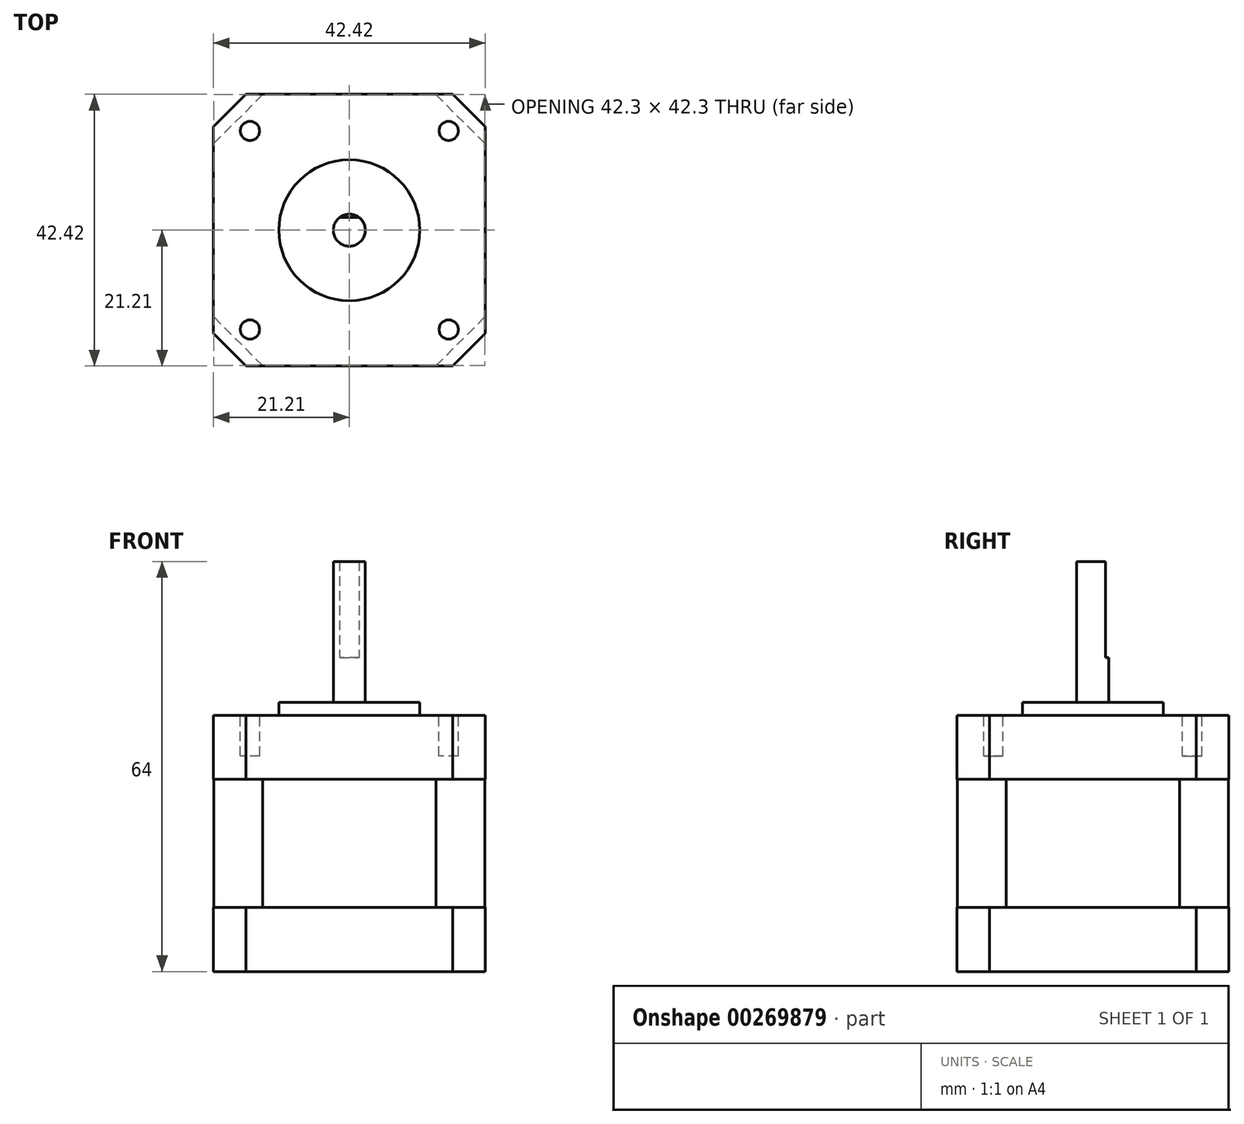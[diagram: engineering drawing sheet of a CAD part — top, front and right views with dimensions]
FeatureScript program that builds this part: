
annotation { "Feature Type Name" : "Feature", "Feature Type Description" : "" }
export const myFeature = defineFeature(function(context is Context, id is Id, definition is map)
    precondition{}
    {
        {
            var Q0;
            Q0=qCreatedBy(makeId("Top.planeOp"),FACE);
            var sketch = newSketch(context, id + "F0", { "sketchPlane" : qUnion([Q0])});
            skLineSegment(sketch, "E0.bottom", {"start": v(-21.15, 21.15) * mm, "end": v(21.15, 21.15) * mm});
            skLineSegment(sketch, "E0.top", {"start": v(-21.15, -21.15) * mm, "end": v(21.15, -21.15) * mm});
            skLineSegment(sketch, "E0.left", {"start": v(-21.15, 21.15) * mm, "end": v(-21.15, -21.15) * mm});
            skLineSegment(sketch, "E0.right", {"start": v(21.15, 21.15) * mm, "end": v(21.15, -21.15) * mm});
            skPoint(sketch, "E1", {"position": v(-21.15, 0) * mm});
            skPoint(sketch, "E2", {"position": v(0, 21.15) * mm});
            skSolve(sketch);
        }
        {
            var Q0;
            Q0=makeQuery(id+"F0.imprint","IMPRINT",FACE,{"disambiguationData":[TD([[makeQuery(id+"F0.imprint","IMPRINT",EDGE,{"derivedFrom":sQuery(id+"F0.wireOp",EDGE,"E0.bottom")}),-1.0]])]});
            extrude(context, id + "F1", {"entities" : qUnion([Q0]), "endBound" : BoundingType.SYMMETRIC, "depth" : 20 * mm});
        }
        {
            var Q0;
            Q0=makeQuery(id+"F1.opExtrude","SWEPT_EDGE",EDGE,{"disambiguationData":[OSD([sQuery(id+"F0.wireOp",EDGE,"E0.bottom"),sQuery(id+"F0.wireOp",EDGE,"E0.right")])]});
            var Q1;
            Q1=makeQuery(id+"F1.opExtrude","SWEPT_EDGE",EDGE,{"disambiguationData":[OSD([sQuery(id+"F0.wireOp",EDGE,"E0.bottom"),sQuery(id+"F0.wireOp",EDGE,"E0.left")])]});
            var Q2;
            Q2=makeQuery(id+"F1.opExtrude","SWEPT_EDGE",EDGE,{"disambiguationData":[OSD([sQuery(id+"F0.wireOp",EDGE,"E0.top"),sQuery(id+"F0.wireOp",EDGE,"E0.left")])]});
            var Q3;
            Q3=makeQuery(id+"F1.opExtrude","SWEPT_EDGE",EDGE,{"disambiguationData":[OSD([sQuery(id+"F0.wireOp",EDGE,"E0.top"),sQuery(id+"F0.wireOp",EDGE,"E0.right")])]});
            chamfer(context, id + "F2", {"entities" : qUnion([Q0, Q1, Q2, Q3]), "width" : 7.62 * mm, "tangentPropagation" : true});
        }
        {
            var Q0;
            Q0=makeQuery(id+"F1.opExtrude","CAP_FACE",FACE,{"disambiguationData":[OSD([sQuery(id+"F0.wireOp",EDGE,"E0.bottom"),sQuery(id+"F0.wireOp",EDGE,"E0.top"),sQuery(id+"F0.wireOp",EDGE,"E0.left"),sQuery(id+"F0.wireOp",EDGE,"E0.right")])],"isStart":false});
            var sketch = newSketch(context, id + "F3", { "sketchPlane" : qUnion([Q0])});
            skLineSegment(sketch, "E3.bottom", {"start": v(-21.2, 21.2) * mm, "end": v(21.2, 21.2) * mm});
            skLineSegment(sketch, "E3.top", {"start": v(-21.2, -21.2) * mm, "end": v(21.2, -21.2) * mm});
            skLineSegment(sketch, "E3.left", {"start": v(-21.2, 21.2) * mm, "end": v(-21.2, -21.2) * mm});
            skLineSegment(sketch, "E3.right", {"start": v(21.2, 21.2) * mm, "end": v(21.2, -21.2) * mm});
            skSolve(sketch);
        }
        {
            var Q0;
            {var subQ0=sQuery(id+"F0.wireOp",EDGE,"E0.top");var subQ1=sQuery(id+"F0.wireOp",EDGE,"E0.right");var subQ2=sQuery(id+"F0.wireOp",EDGE,"E0.bottom");var subQ3=sQuery(id+"F0.wireOp",EDGE,"E0.left");var subQ4=makeQuery(id+"F1.opExtrude","CAP_FACE",FACE,{"disambiguationData":[OSD([subQ2,subQ0,subQ3,subQ1])],"isStart":false});var subQ8=makeQuery(id+"F2.opChamfer","BLEND_EDGE",EDGE,{"blendedFrom":[makeQuery(id+"F1.opExtrude","SWEPT_EDGE",EDGE,{"disambiguationData":[OSD([subQ2,subQ3])]}),subQ4],"blendedInto":[subQ4]});Q0=makeQuery(id+"F3.imprint","IMPRINT",FACE,{"disambiguationData":[TD([[makeQuery(id+"F3.imprint","IMPRINT",EDGE,{"derivedFrom":subQ8}),1.0]])]});}
            var Q1;
            {var subQ0=sQuery(id+"F0.wireOp",EDGE,"E0.bottom");var subQ1=sQuery(id+"F0.wireOp",EDGE,"E0.right");var subQ2=makeQuery(id+"F2.opChamfer","BLEND_EDGE",EDGE,{"blendedFrom":[makeQuery(id+"F1.opExtrude","SWEPT_EDGE",EDGE,{"disambiguationData":[OSD([subQ0,subQ1])]}),makeQuery(id+"F1.opExtrude","CAP_FACE",FACE,{"disambiguationData":[OSD([subQ0,sQuery(id+"F0.wireOp",EDGE,"E0.top"),sQuery(id+"F0.wireOp",EDGE,"E0.left"),subQ1])],"isStart":false})],"blendedInto":[makeQuery(id+"F1.opExtrude","CAP_FACE",FACE,{"disambiguationData":[OSD([subQ0,sQuery(id+"F0.wireOp",EDGE,"E0.top"),sQuery(id+"F0.wireOp",EDGE,"E0.left"),subQ1])],"isStart":false})]});Q1=makeQuery(id+"F3.imprint","IMPRINT",FACE,{"disambiguationData":[TD([[makeQuery(id+"F3.imprint","IMPRINT",EDGE,{"derivedFrom":subQ2}),-1.0]])]});}
            var Q2;
            {var subQ0=sQuery(id+"F0.wireOp",EDGE,"E0.bottom");var subQ1=sQuery(id+"F0.wireOp",EDGE,"E0.left");var subQ2=makeQuery(id+"F2.opChamfer","BLEND_EDGE",EDGE,{"blendedFrom":[makeQuery(id+"F1.opExtrude","SWEPT_EDGE",EDGE,{"disambiguationData":[OSD([subQ0,subQ1])]}),makeQuery(id+"F1.opExtrude","CAP_FACE",FACE,{"disambiguationData":[OSD([subQ0,sQuery(id+"F0.wireOp",EDGE,"E0.top"),subQ1,sQuery(id+"F0.wireOp",EDGE,"E0.right")])],"isStart":false})],"blendedInto":[makeQuery(id+"F1.opExtrude","CAP_FACE",FACE,{"disambiguationData":[OSD([subQ0,sQuery(id+"F0.wireOp",EDGE,"E0.top"),subQ1,sQuery(id+"F0.wireOp",EDGE,"E0.right")])],"isStart":false})]});Q2=makeQuery(id+"F3.imprint","IMPRINT",FACE,{"disambiguationData":[TD([[makeQuery(id+"F3.imprint","IMPRINT",EDGE,{"derivedFrom":subQ2}),-1.0]])]});}
            var Q3;
            {var subQ0=sQuery(id+"F0.wireOp",EDGE,"E0.top");var subQ1=sQuery(id+"F0.wireOp",EDGE,"E0.left");var subQ2=makeQuery(id+"F2.opChamfer","BLEND_EDGE",EDGE,{"blendedFrom":[makeQuery(id+"F1.opExtrude","SWEPT_EDGE",EDGE,{"disambiguationData":[OSD([subQ0,subQ1])]}),makeQuery(id+"F1.opExtrude","CAP_FACE",FACE,{"disambiguationData":[OSD([sQuery(id+"F0.wireOp",EDGE,"E0.bottom"),subQ0,subQ1,sQuery(id+"F0.wireOp",EDGE,"E0.right")])],"isStart":false})],"blendedInto":[makeQuery(id+"F1.opExtrude","CAP_FACE",FACE,{"disambiguationData":[OSD([sQuery(id+"F0.wireOp",EDGE,"E0.bottom"),subQ0,subQ1,sQuery(id+"F0.wireOp",EDGE,"E0.right")])],"isStart":false})]});Q3=makeQuery(id+"F3.imprint","IMPRINT",FACE,{"disambiguationData":[TD([[makeQuery(id+"F3.imprint","IMPRINT",EDGE,{"derivedFrom":subQ2}),-1.0]])]});}
            var Q4;
            {var subQ0=sQuery(id+"F0.wireOp",EDGE,"E0.top");var subQ1=sQuery(id+"F0.wireOp",EDGE,"E0.right");var subQ2=makeQuery(id+"F2.opChamfer","BLEND_EDGE",EDGE,{"blendedFrom":[makeQuery(id+"F1.opExtrude","SWEPT_EDGE",EDGE,{"disambiguationData":[OSD([subQ0,subQ1])]}),makeQuery(id+"F1.opExtrude","CAP_FACE",FACE,{"disambiguationData":[OSD([sQuery(id+"F0.wireOp",EDGE,"E0.bottom"),subQ0,sQuery(id+"F0.wireOp",EDGE,"E0.left"),subQ1])],"isStart":false})],"blendedInto":[makeQuery(id+"F1.opExtrude","CAP_FACE",FACE,{"disambiguationData":[OSD([sQuery(id+"F0.wireOp",EDGE,"E0.bottom"),subQ0,sQuery(id+"F0.wireOp",EDGE,"E0.left"),subQ1])],"isStart":false})]});Q4=makeQuery(id+"F3.imprint","IMPRINT",FACE,{"disambiguationData":[TD([[makeQuery(id+"F3.imprint","IMPRINT",EDGE,{"derivedFrom":subQ2}),-1.0]])]});}
            extrude(context, id + "F4", {"entities" : qUnion([Q0, Q1, Q2, Q3, Q4]), "operationType" : NewBodyOperationType.ADD, "depth" : 10 * mm});
        }
        {
            var Q0;
            Q0=makeQuery(id+"F4.opExtrude","SWEPT_EDGE",EDGE,{"disambiguationData":[OSD([sQuery(id+"F3.wireOp",EDGE,"E3.bottom"),sQuery(id+"F3.wireOp",EDGE,"E3.right")])]});
            var Q1;
            Q1=makeQuery(id+"F4.opExtrude","SWEPT_EDGE",EDGE,{"disambiguationData":[OSD([sQuery(id+"F3.wireOp",EDGE,"E3.bottom"),sQuery(id+"F3.wireOp",EDGE,"E3.left")])]});
            var Q2;
            Q2=makeQuery(id+"F4.opExtrude","SWEPT_EDGE",EDGE,{"disambiguationData":[OSD([sQuery(id+"F3.wireOp",EDGE,"E3.top"),sQuery(id+"F3.wireOp",EDGE,"E3.left")])]});
            var Q3;
            Q3=makeQuery(id+"F4.opExtrude","SWEPT_EDGE",EDGE,{"disambiguationData":[OSD([sQuery(id+"F3.wireOp",EDGE,"E3.top"),sQuery(id+"F3.wireOp",EDGE,"E3.right")])]});
            chamfer(context, id + "F5", {"entities" : qUnion([Q0, Q1, Q2, Q3]), "width" : 5.08 * mm, "tangentPropagation" : true});
        }
        {
            var Q0;
            Q0=makeQuery(id+"F1.opExtrude","CAP_FACE",FACE,{"disambiguationData":[OSD([sQuery(id+"F0.wireOp",EDGE,"E0.bottom"),sQuery(id+"F0.wireOp",EDGE,"E0.top"),sQuery(id+"F0.wireOp",EDGE,"E0.left"),sQuery(id+"F0.wireOp",EDGE,"E0.right")])],"isStart":true});
            var sketch = newSketch(context, id + "F6", { "sketchPlane" : qUnion([Q0])});
            skLineSegment(sketch, "E4.0.0", {"start": v(-16.13, 21.2) * mm, "end": v(16.13, 21.2) * mm});
            skLineSegment(sketch, "E4.0.1", {"start": v(16.13, 21.2) * mm, "end": v(21.2, 16.13) * mm});
            skLineSegment(sketch, "E4.0.2", {"start": v(21.2, -16.13) * mm, "end": v(21.2, 16.13) * mm});
            skLineSegment(sketch, "E4.0.3", {"start": v(21.2, -16.13) * mm, "end": v(16.13, -21.2) * mm});
            skLineSegment(sketch, "E4.0.4", {"start": v(-16.13, -21.2) * mm, "end": v(16.13, -21.2) * mm});
            skLineSegment(sketch, "E4.0.5", {"start": v(-16.13, -21.2) * mm, "end": v(-21.2, -16.13) * mm});
            skLineSegment(sketch, "E4.0.6", {"start": v(-21.2, -16.13) * mm, "end": v(-21.2, 16.13) * mm});
            skLineSegment(sketch, "E4.0.7", {"start": v(-21.2, 16.13) * mm, "end": v(-16.13, 21.2) * mm});
            skSolve(sketch);
        }
        {
            var Q0;
            {var subQ3=sQuery(id+"F6.wireOp",EDGE,"E4.0.7");Q0=makeQuery(id+"F6.imprint","IMPRINT",FACE,{"disambiguationData":[TD([[makeQuery(id+"F6.imprint","IMPRINT",EDGE,{"derivedFrom":subQ3}),-1.0]])]});}
            var Q1;
            {var subQ4=sQuery(id+"F6.wireOp",EDGE,"E4.0.1");Q1=makeQuery(id+"F6.imprint","IMPRINT",FACE,{"disambiguationData":[TD([[makeQuery(id+"F6.imprint","IMPRINT",EDGE,{"derivedFrom":subQ4}),-1.0]])]});}
            var Q2;
            {var subQ4=sQuery(id+"F6.wireOp",EDGE,"E4.0.3");Q2=makeQuery(id+"F6.imprint","IMPRINT",FACE,{"disambiguationData":[TD([[makeQuery(id+"F6.imprint","IMPRINT",EDGE,{"derivedFrom":subQ4}),-1.0]])]});}
            var Q3;
            {var subQ4=sQuery(id+"F6.wireOp",EDGE,"E4.0.5");Q3=makeQuery(id+"F6.imprint","IMPRINT",FACE,{"disambiguationData":[TD([[makeQuery(id+"F6.imprint","IMPRINT",EDGE,{"derivedFrom":subQ4}),-1.0]])]});}
            var Q4;
            {var subQ0=sQuery(id+"F0.wireOp",EDGE,"E0.top");var subQ1=sQuery(id+"F0.wireOp",EDGE,"E0.right");var subQ2=sQuery(id+"F0.wireOp",EDGE,"E0.bottom");var subQ3=sQuery(id+"F0.wireOp",EDGE,"E0.left");var subQ4=makeQuery(id+"F1.opExtrude","CAP_FACE",FACE,{"disambiguationData":[OSD([subQ2,subQ0,subQ3,subQ1])],"isStart":true});var subQ8=makeQuery(id+"F2.opChamfer","BLEND_EDGE",EDGE,{"blendedFrom":[makeQuery(id+"F1.opExtrude","SWEPT_EDGE",EDGE,{"disambiguationData":[OSD([subQ2,subQ3])]}),subQ4],"blendedInto":[subQ4]});Q4=makeQuery(id+"F6.imprint","IMPRINT",FACE,{"disambiguationData":[TD([[makeQuery(id+"F6.imprint","IMPRINT",EDGE,{"derivedFrom":subQ8}),1.0]])]});}
            extrude(context, id + "F7", {"entities" : qUnion([Q0, Q1, Q2, Q3, Q4]), "operationType" : NewBodyOperationType.ADD, "depth" : 10 * mm});
        }
        {
            var Q0;
            Q0=makeQuery(id+"F4.opExtrude","CAP_FACE",FACE,{"disambiguationData":[OSD([sQuery(id+"F3.wireOp",EDGE,"E3.bottom"),sQuery(id+"F3.wireOp",EDGE,"E3.top"),sQuery(id+"F3.wireOp",EDGE,"E3.left"),sQuery(id+"F3.wireOp",EDGE,"E3.right")])],"isStart":false});
            var sketch = newSketch(context, id + "F8", { "sketchPlane" : qUnion([Q0])});
            skCircle(sketch, "E5", {"center": v(0, 0) * mm, "radius": 11 * mm});
            skSolve(sketch);
        }
        {
            var Q0;
            Q0=makeQuery(id+"F8.imprint","IMPRINT",FACE,{"disambiguationData":[TD([[makeQuery(id+"F8.imprint","IMPRINT",EDGE,{"derivedFrom":sQuery(id+"F8.wireOp",EDGE,"E5")}),1.0]])]});
            extrude(context, id + "F9", {"entities" : qUnion([Q0]), "operationType" : NewBodyOperationType.ADD, "depth" : 2 * mm});
        }
        {
            var Q0;
            Q0=makeQuery(id+"F9.opExtrude","CAP_FACE",FACE,{"disambiguationData":[OSD([sQuery(id+"F8.wireOp",EDGE,"E5")])],"isStart":false});
            var sketch = newSketch(context, id + "F10", { "sketchPlane" : qUnion([Q0])});
            skCircle(sketch, "E6", {"center": v(0, 0) * mm, "radius": 2.5 * mm});
            skSolve(sketch);
        }
        {
            var Q0;
            Q0=makeQuery(id+"F10.imprint","IMPRINT",FACE,{"disambiguationData":[TD([[makeQuery(id+"F10.imprint","IMPRINT",EDGE,{"derivedFrom":sQuery(id+"F10.wireOp",EDGE,"E6")}),1.0]])]});
            extrude(context, id + "F11", {"entities" : qUnion([Q0]), "operationType" : NewBodyOperationType.ADD, "depth" : 22 * mm});
        }
        {
            var Q0;
            Q0=makeQuery(id+"F11.opExtrude","CAP_FACE",FACE,{"disambiguationData":[OSD([sQuery(id+"F10.wireOp",EDGE,"E6")])],"isStart":false});
            var sketch = newSketch(context, id + "F12", { "sketchPlane" : qUnion([Q0])});
            skLineSegment(sketch, "E7.bottom", {"start": v(-2.63, 2.93) * mm, "end": v(2.62, 2.93) * mm});
            skLineSegment(sketch, "E7.top", {"start": v(-2.63, 2) * mm, "end": v(2.62, 2) * mm});
            skLineSegment(sketch, "E7.left", {"start": v(-2.63, 2.93) * mm, "end": v(-2.63, 2) * mm});
            skLineSegment(sketch, "E7.right", {"start": v(2.62, 2.93) * mm, "end": v(2.62, 2) * mm});
            skSolve(sketch);
        }
        {
            var Q0;
            {var subQ0=makeQuery(id+"F11.opExtrude","CAP_EDGE",EDGE,{"disambiguationData":[OSD([sQuery(id+"F10.wireOp",EDGE,"E6")])],"isStart":false});var subQ1=sQuery(id+"F12.wireOp",EDGE,"E7.top");var subQ3=makeQuery(id+"F12.imprint","INTERSECT",VERTEX,{"disambiguationData":[OD(0.0)],"derivedFrom":[subQ0,subQ1]});Q0=qUnion([makeQuery(id+"F12.imprint","IMPRINT",FACE,{"disambiguationData":[TD([[makeQuery(id+"F12.imprint","IMPRINT",EDGE,{"derivedFrom":sQuery(id+"F12.wireOp",EDGE,"E7.bottom")}),-1.0]])]}),makeQuery(id+"F12.imprint","IMPRINT",FACE,{"disambiguationData":[TD([[makeQuery(id+"F12.imprint","IMPRINT",EDGE,{"disambiguationData":[TD([[subQ3,-1.0]])],"derivedFrom":subQ1}),1.0]])]})]);}
            extrude(context, id + "F13", {"entities" : qUnion([Q0]), "operationType" : NewBodyOperationType.REMOVE, "oppositeDirection" : true, "depth" : 15 * mm});
        }
        {
            var Q0;
            Q0=makeQuery(id+"F4.opExtrude","CAP_FACE",FACE,{"disambiguationData":[OSD([sQuery(id+"F3.wireOp",EDGE,"E3.bottom"),sQuery(id+"F3.wireOp",EDGE,"E3.top"),sQuery(id+"F3.wireOp",EDGE,"E3.left"),sQuery(id+"F3.wireOp",EDGE,"E3.right")])],"isStart":false});
            var sketch = newSketch(context, id + "F14", { "sketchPlane" : qUnion([Q0])});
            skCircle(sketch, "E8", {"center": v(-15.5, 15.5) * mm, "radius": 1.5 * mm});
            skCircle(sketch, "E9", {"center": v(15.5, 15.5) * mm, "radius": 1.5 * mm});
            skCircle(sketch, "E10", {"center": v(15.5, -15.5) * mm, "radius": 1.5 * mm});
            skCircle(sketch, "E11", {"center": v(-15.5, -15.5) * mm, "radius": 1.5 * mm});
            skLineSegment(sketch, "E12", {"start": v(-15.5, 0) * mm, "end": v(15.5, 0) * mm, "construction": true});
            skLineSegment(sketch, "E13", {"start": v(0, -15.5) * mm, "end": v(0, 15.5) * mm, "construction": true});
            skLineSegment(sketch, "E14.rect.bottom", {"start": v(-15.5, 15.5) * mm, "end": v(15.5, 15.5) * mm, "construction": true});
            skLineSegment(sketch, "E14.rect.top", {"start": v(-15.5, -15.5) * mm, "end": v(15.5, -15.5) * mm, "construction": true});
            skLineSegment(sketch, "E14.rect.left", {"start": v(-15.5, 15.5) * mm, "end": v(-15.5, -15.5) * mm, "construction": true});
            skLineSegment(sketch, "E14.rect.right", {"start": v(15.5, 15.5) * mm, "end": v(15.5, -15.5) * mm, "construction": true});
            skPoint(sketch, "E14.rect.middle", {"position": v(0, 0) * mm});
            skPoint(sketch, "E15", {"position": v(0, 15.5) * mm});
            skSolve(sketch);
        }
        {
            var Q0;
            {Q0=qUnion([makeQuery(id+"F14.imprint","IMPRINT",FACE,{"disambiguationData":[TD([[makeQuery(id+"F14.imprint","IMPRINT",EDGE,{"derivedFrom":sQuery(id+"F14.wireOp",EDGE,"E8")}),1.0]])]}),makeQuery(id+"F14.imprint","IMPRINT",FACE,{"disambiguationData":[TD([[makeQuery(id+"F14.imprint","IMPRINT",EDGE,{"derivedFrom":sQuery(id+"F14.wireOp",EDGE,"E9")}),1.0]])]}),makeQuery(id+"F14.imprint","IMPRINT",FACE,{"disambiguationData":[TD([[makeQuery(id+"F14.imprint","IMPRINT",EDGE,{"derivedFrom":sQuery(id+"F14.wireOp",EDGE,"E10")}),1.0]])]}),makeQuery(id+"F14.imprint","IMPRINT",FACE,{"disambiguationData":[TD([[makeQuery(id+"F14.imprint","IMPRINT",EDGE,{"derivedFrom":sQuery(id+"F14.wireOp",EDGE,"E11")}),1.0]])]})]);}
            extrude(context, id + "F15", {"entities" : qUnion([Q0]), "operationType" : NewBodyOperationType.REMOVE, "oppositeDirection" : true, "depth" : 6.35 * mm});
        }
    });
